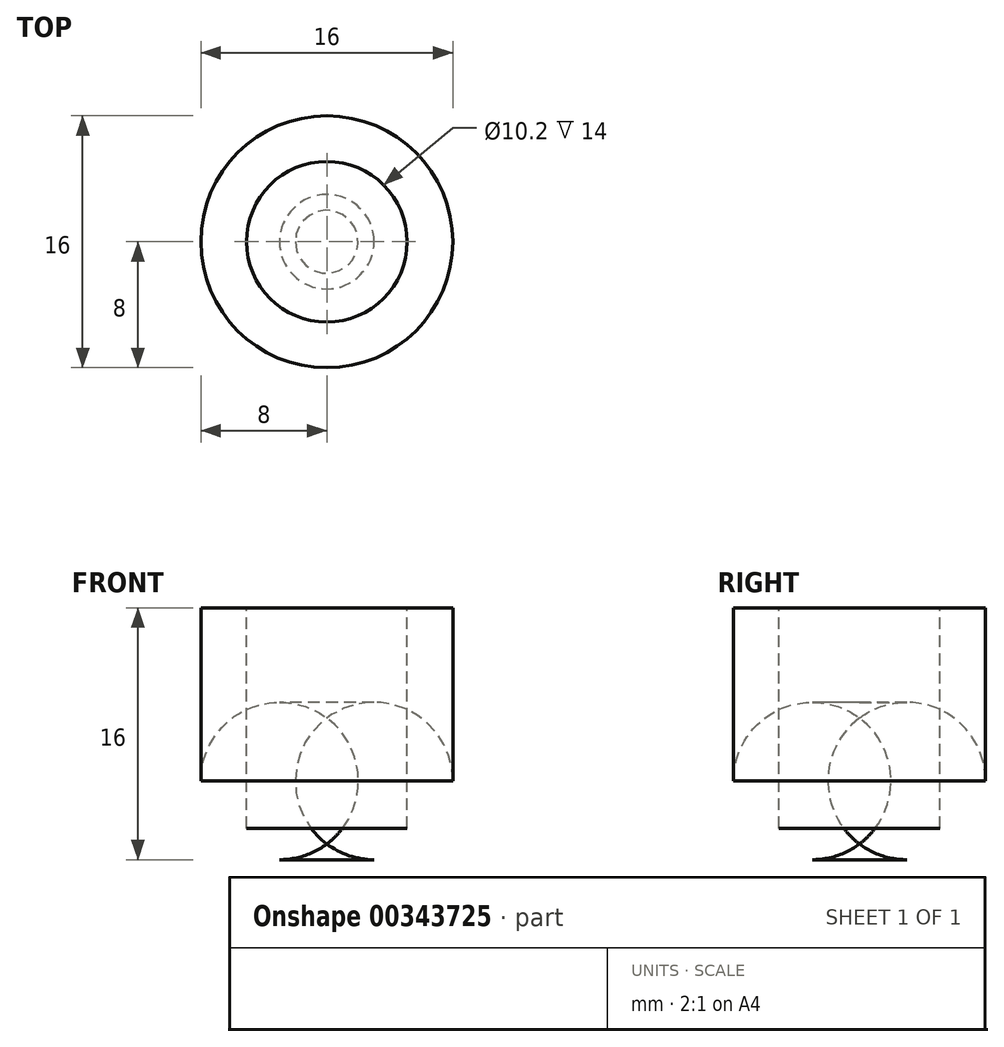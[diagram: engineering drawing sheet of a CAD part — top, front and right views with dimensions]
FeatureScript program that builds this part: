
annotation { "Feature Type Name" : "Feature", "Feature Type Description" : "" }
export const myFeature = defineFeature(function(context is Context, id is Id, definition is map)
    precondition{}
    {
        {
            var Q0;
            Q0=qCreatedBy(makeId("Top.planeOp"),FACE);
            var sketch = newSketch(context, id + "F0", { "sketchPlane" : qUnion([Q0])});
            skCircle(sketch, "E0", {"center": v(0, 0) * mm, "radius": 8 * mm});
            skSolve(sketch);
        }
        {
            var Q0;
            Q0=makeQuery(id+"F0.imprint","IMPRINT",FACE,{"disambiguationData":[TD([[makeQuery(id+"F0.imprint","IMPRINT",EDGE,{"derivedFrom":sQuery(id+"F0.wireOp",EDGE,"E0")}),1.0]])]});
            extrude(context, id + "F1", {"entities" : qUnion([Q0]), "depth" : 16 * mm});
        }
        {
            var Q0;
            Q0=makeQuery(id+"F1.opExtrude","CAP_FACE",FACE,{"disambiguationData":[OSD([sQuery(id+"F0.wireOp",EDGE,"E0")])],"isStart":false});
            var sketch = newSketch(context, id + "F2", { "sketchPlane" : qUnion([Q0])});
            skCircle(sketch, "E1", {"center": v(0, 0) * mm, "radius": 5.1 * mm});
            skSolve(sketch);
        }
        {
            var Q0;
            Q0 = qSketchRegion(id + "F2", true);
            extrude(context, id + "F3", {"entities" : qUnion([Q0]), "operationType" : NewBodyOperationType.REMOVE, "oppositeDirection" : true, "depth" : 14 * mm});
        }
        {
            var Q0;
            Q0=makeQuery(id+"F1.opExtrude","CAP_EDGE",EDGE,{"disambiguationData":[OSD([sQuery(id+"F0.wireOp",EDGE,"E0")])],"isStart":true});
            fillet(context, id + "F4", {"entities" : qUnion([Q0]), "radius" : 5 * mm, "tangentPropagation" : true, "allowEdgeOverflow" : false});
        }
    });
